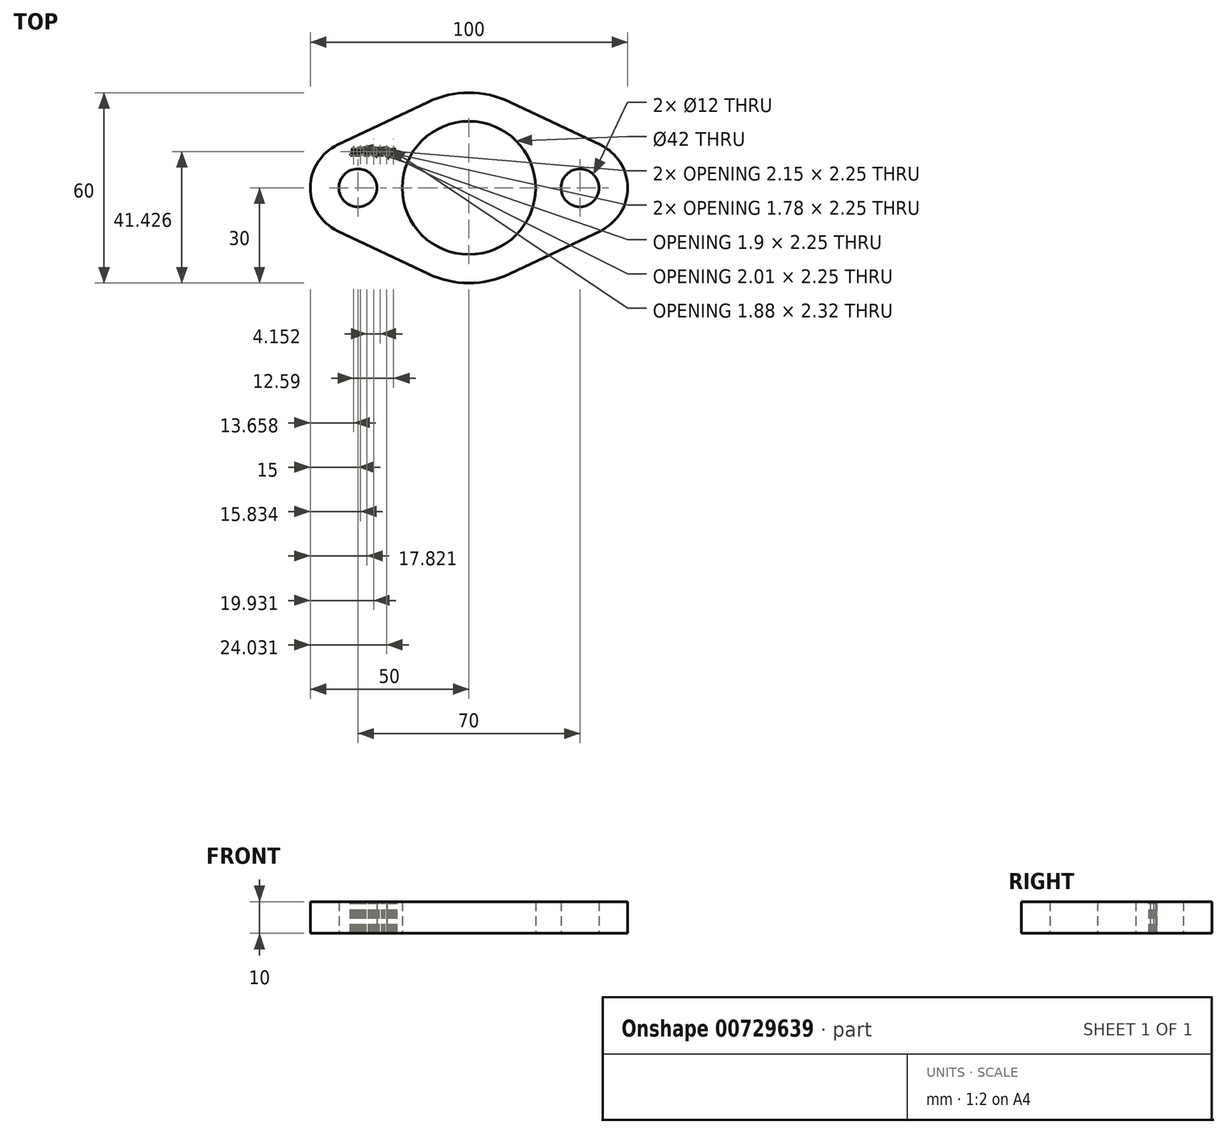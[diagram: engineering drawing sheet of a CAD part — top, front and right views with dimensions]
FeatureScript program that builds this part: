
annotation { "Feature Type Name" : "Feature", "Feature Type Description" : "" }
export const myFeature = defineFeature(function(context is Context, id is Id, definition is map)
    precondition{}
    {
        {
            var Q0;
            Q0=qCreatedBy(makeId("Top.planeOp"),FACE);
            var sketch = newSketch(context, id + "F0", { "sketchPlane" : qUnion([Q0])});
            skCircle(sketch, "E0", {"center": v(0, 0) * mm, "radius": 21 * mm});
            skArc(sketch, "E1", {"start": v(12.86, 27.1) * mm, "mid": v(0, 30) * mm, "end": v(-12.86, 27.1) * mm});
            skCircle(sketch, "E2", {"center": v(35, 0) * mm, "radius": 6 * mm});
            skArc(sketch, "E3", {"start": v(41.43, -13.55) * mm, "mid": v(50, 0) * mm, "end": v(41.43, 13.55) * mm});
            skLineSegment(sketch, "E4", {"start": v(12.86, 27.1) * mm, "end": v(41.43, 13.55) * mm});
            skPoint(sketch, "E5.orphan", {"position": v(0, 38.43) * mm});
            skLineSegment(sketch, "E6", {"start": v(41.43, -13.55) * mm, "end": v(12.86, -27.1) * mm});
            skLineSegment(sketch, "E7", {"start": v(0, 0) * mm, "end": v(35, 0) * mm});
            skArc(sketch, "E8.trimOffspring", {"start": v(-12.86, -27.1) * mm, "mid": v(0, -30) * mm, "end": v(12.86, -27.1) * mm});
            skCircle(sketch, "E9", {"center": v(-35, 0) * mm, "radius": 6 * mm});
            skArc(sketch, "E10", {"start": v(-41.43, 13.55) * mm, "mid": v(-50, 0) * mm, "end": v(-41.43, -13.55) * mm});
            skLineSegment(sketch, "E11", {"start": v(-41.43, 13.55) * mm, "end": v(-12.86, 27.1) * mm});
            skLineSegment(sketch, "E12", {"start": v(-41.43, -13.55) * mm, "end": v(-12.86, -27.1) * mm});
            skSolve(sketch);
        }
        {
            var Q0;
            Q0 = qSketchRegion(id + "F0", true);
            extrude(context, id + "F1", {"entities" : qUnion([Q0]), "depth" : 10 * mm, "offsetDistance" : 25 * mm});
        }
        {
            var Q0;
            Q0=makeQuery(id+"F1.opExtrude","CAP_FACE",FACE,{"disambiguationData":[OSD([sQuery(id+"F0.wireOp",EDGE,"E1"),sQuery(id+"F0.wireOp",EDGE,"E2"),sQuery(id+"F0.wireOp",EDGE,"E3"),sQuery(id+"F0.wireOp",EDGE,"E4"),sQuery(id+"F0.wireOp",EDGE,"E6"),sQuery(id+"F0.wireOp",EDGE,"E0"),sQuery(id+"F0.wireOp",EDGE,"E8.trimOffspring"),sQuery(id+"F0.wireOp",EDGE,"E9"),sQuery(id+"F0.wireOp",EDGE,"E10"),sQuery(id+"F0.wireOp",EDGE,"E11"),sQuery(id+"F0.wireOp",EDGE,"E12")])],"isStart":false});
            var sketch = newSketch(context, id + "F2", { "sketchPlane" : qUnion([Q0])});
            skText(sketch, "E13", { "text": "APETEGA\n", "fontName": "RobotoSlab-Bold.ttf"});
            const initialGuessF2  = {"E13": [-0.03748, 0.0103, 1, 0, 0.00228]};
            skSetInitialGuess(sketch, initialGuessF2);
            skSolve(sketch);
        }
        {
            var Q0;
            Q0 = qSketchRegion(id + "F2", true);
            var Q1;
            Q1 = qSketchRegion(id + "F0", true);
            extrude(context, id + "F3", {"entities" : qUnion([Q0, Q1]), "operationType" : NewBodyOperationType.REMOVE, "oppositeDirection" : true, "depth" : 10 * mm, "offsetDistance" : 25 * mm});
        }
    });
